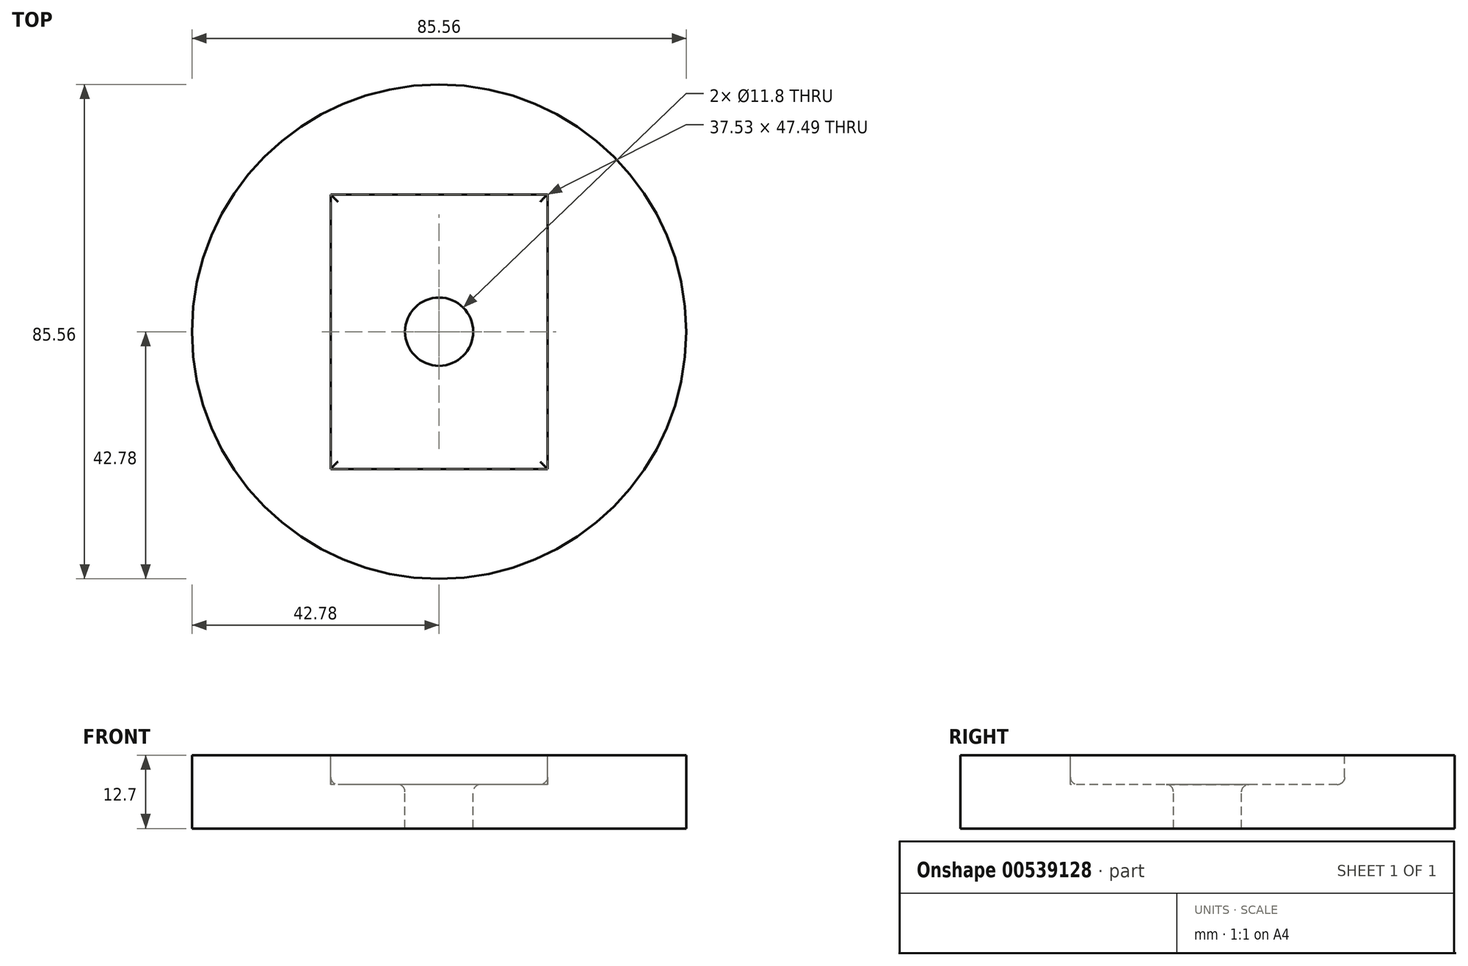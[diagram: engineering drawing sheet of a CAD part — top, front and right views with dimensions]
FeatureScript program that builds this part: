
annotation { "Feature Type Name" : "Feature", "Feature Type Description" : "" }
export const myFeature = defineFeature(function(context is Context, id is Id, definition is map)
    precondition{}
    {
        {
            var Q0;
            Q0=qCreatedBy(makeId("Top.planeOp"),FACE);
            var sketch = newSketch(context, id + "F0", { "sketchPlane" : qUnion([Q0])});
            skCircle(sketch, "E0", {"center": v(0, 0) * mm, "radius": 42.78 * mm});
            skSolve(sketch);
        }
        {
            var Q0;
            Q0 = qSketchRegion(id + "F0", true);
            extrude(context, id + "F1", {"entities" : qUnion([Q0]), "depth" : 12.7 * mm, "offsetDistance" : 25.4 * mm});
        }
        {
            var Q0;
            Q0=makeQuery(id+"F1.opExtrude","CAP_FACE",FACE,{"disambiguationData":[OSD([sQuery(id+"F0.wireOp",EDGE,"E0")])],"isStart":false});
            var sketch = newSketch(context, id + "F2", { "sketchPlane" : qUnion([Q0])});
            skLineSegment(sketch, "E1.bottom", {"start": v(18.76, 23.74) * mm, "end": v(-18.76, 23.74) * mm});
            skLineSegment(sketch, "E1.top", {"start": v(18.76, -23.74) * mm, "end": v(-18.76, -23.74) * mm});
            skLineSegment(sketch, "E1.left", {"start": v(18.76, 23.74) * mm, "end": v(18.76, -23.74) * mm});
            skLineSegment(sketch, "E1.right", {"start": v(-18.76, 23.74) * mm, "end": v(-18.76, -23.74) * mm});
            skPoint(sketch, "E1.middle", {"position": v(0, 0) * mm});
            skSolve(sketch);
        }
        {
            var Q0;
            Q0 = qSketchRegion(id + "F2", true);
            extrude(context, id + "F3", {"entities" : qUnion([Q0]), "operationType" : NewBodyOperationType.REMOVE, "oppositeDirection" : true, "depth" : 5.08 * mm, "offsetDistance" : 25.4 * mm});
        }
        {
            var Q0;
            Q0=makeQuery(id+"F3.boolean.opBoolean","COPY",FACE,{"derivedFrom":makeQuery(id+"F3.opExtrude","CAP_FACE",FACE,{"disambiguationData":[OSD([sQuery(id+"F2.wireOp",EDGE,"E1.bottom"),sQuery(id+"F2.wireOp",EDGE,"E1.top"),sQuery(id+"F2.wireOp",EDGE,"E1.left"),sQuery(id+"F2.wireOp",EDGE,"E1.right")])],"isStart":false})});
            var sketch = newSketch(context, id + "F4", { "sketchPlane" : qUnion([Q0])});
            skCircle(sketch, "E2", {"center": v(0, 0) * mm, "radius": 5.9 * mm});
            skSolve(sketch);
        }
        {
            var Q0;
            Q0 = qSketchRegion(id + "F4", true);
            extrude(context, id + "F5", {"entities" : qUnion([Q0]), "operationType" : NewBodyOperationType.REMOVE, "oppositeDirection" : true, "depth" : 25.4 * mm, "offsetDistance" : 25.4 * mm});
        }
        {
            var Q0;
            Q0=makeQuery(id+"F3.boolean.opBoolean","COPY",EDGE,{"derivedFrom":makeQuery(id+"F3.opExtrude","CAP_EDGE",EDGE,{"disambiguationData":[OSD([sQuery(id+"F2.wireOp",EDGE,"E1.bottom")])],"isStart":false})});
            var Q1;
            Q1=makeQuery(id+"F3.boolean.opBoolean","COPY",FACE,{"derivedFrom":makeQuery(id+"F3.opExtrude","CAP_FACE",FACE,{"disambiguationData":[OSD([sQuery(id+"F2.wireOp",EDGE,"E1.bottom"),sQuery(id+"F2.wireOp",EDGE,"E1.top"),sQuery(id+"F2.wireOp",EDGE,"E1.left"),sQuery(id+"F2.wireOp",EDGE,"E1.right")])],"isStart":false})});
            fillet(context, id + "F6", {"entities" : qUnion([Q0, Q1]), "radius" : 1.27 * mm, "tangentPropagation" : true, "allowEdgeOverflow" : false});
        }
    });
